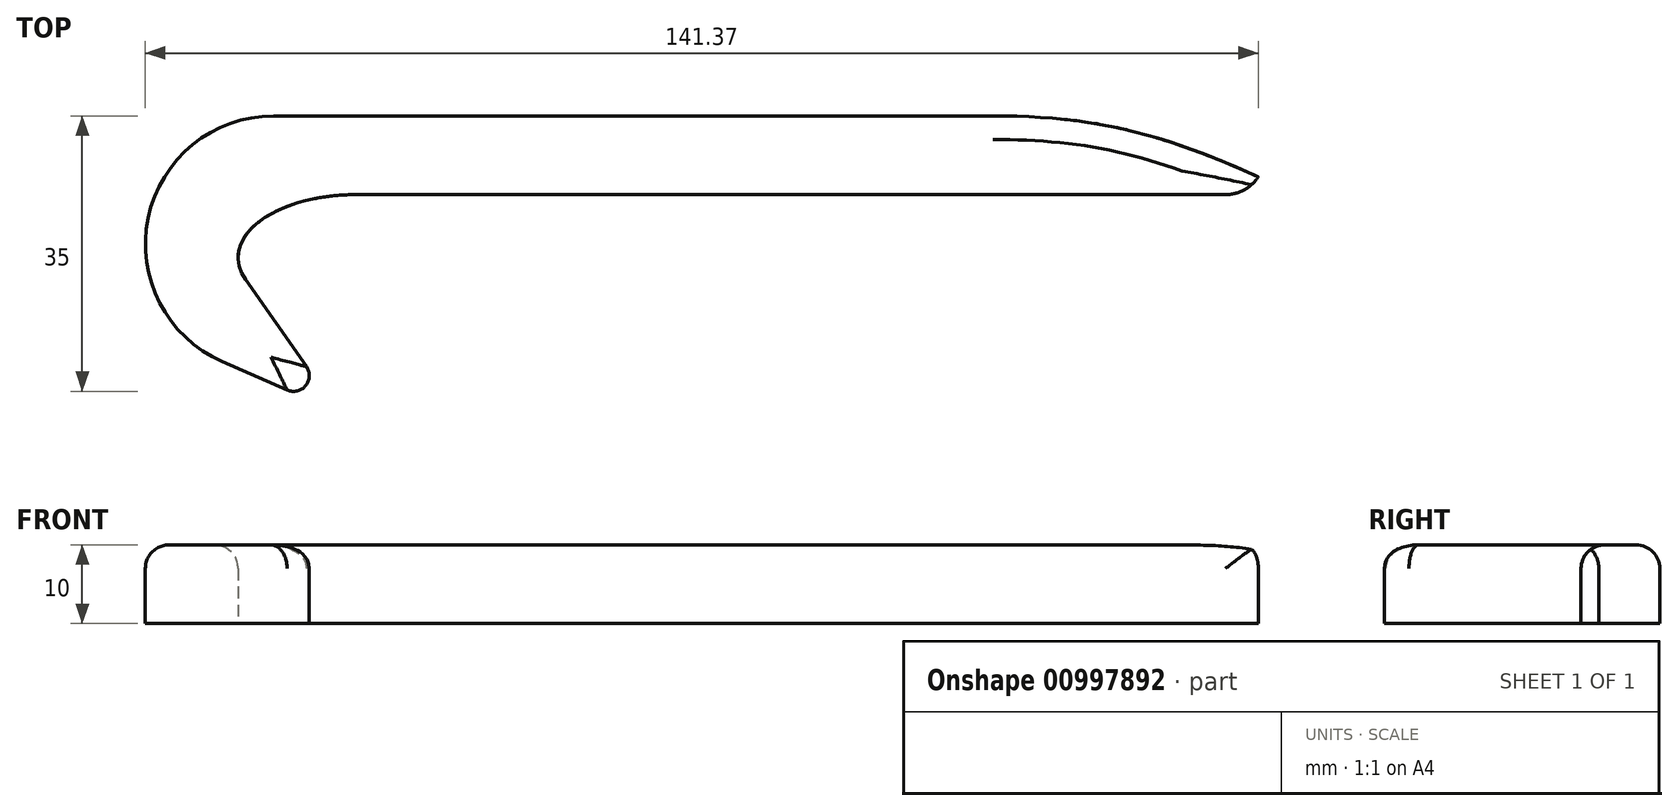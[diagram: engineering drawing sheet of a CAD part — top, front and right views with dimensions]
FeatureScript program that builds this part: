
annotation { "Feature Type Name" : "Feature", "Feature Type Description" : "" }
export const myFeature = defineFeature(function(context is Context, id is Id, definition is map)
    precondition{}
    {
        {
            var Q0;
            Q0=qCreatedBy(makeId("Top.planeOp"),FACE);
            var sketch = newSketch(context, id + "F0", { "sketchPlane" : qUnion([Q0])});
            skLineSegment(sketch, "E0", {"start": v(-59.75, -24.83) * mm, "end": v(-68.01, -21.22) * mm});
            skLineSegment(sketch, "E1", {"start": v(-61.48, 10) * mm, "end": v(0, 10) * mm});
            skLineSegment(sketch, "E2", {"start": v(0, 0) * mm, "end": v(-63.6, 0) * mm});
            skLineSegment(sketch, "E3", {"start": v(-68.12, -6.42) * mm, "end": v(-57.31, -21.85) * mm});
            skPoint(sketch, "E4.visualSharp", {"position": v(-139.32, 10) * mm});
            skArc(sketch, "E4.filletArc", {"start": v(-61.48, 10) * mm, "mid": v(-77.42, -2.95) * mm, "end": v(-68.01, -21.22) * mm});
            skPoint(sketch, "E5.visualSharp", {"position": v(-53.23, -27.69) * mm});
            skArc(sketch, "E5.filletArc", {"start": v(-59.75, -24.83) * mm, "mid": v(-57.4, -24.27) * mm, "end": v(-57.31, -21.85) * mm});
            skPoint(sketch, "E6.visualSharp", {"position": v(-72.61, 0) * mm});
            skLineSegment(sketch, "E7", {"start": v(-36.97, -25) * mm, "end": v(-18.83, -25) * mm, "construction": true});
            skPoint(sketch, "E7.startSnap0", {"position": v(-57.4, -24.27) * mm});
            skLineSegment(sketch, "E8.MirrorCS", {"start": v(0, 0) * mm, "end": v(63.6, 0) * mm});
            skLineSegment(sketch, "E9", {"start": v(0, 10) * mm, "end": v(29.9, 10) * mm});
            skLineSegment(sketch, "E10", {"start": v(63.6, 10) * mm, "end": v(63.6, 0) * mm});
            skEllipse(sketch, "E11", {"center": v(51, -8) * mm, "majorRadius": 15 * mm, "minorRadius": 8 * mm, "majorAxis": v(1, 0)});
            skFitSpline(sketch, "E12.0", {"points": [v(70.9, -9.71) * mm, v(71.05, -8) * mm, v(70.9, -6.29) * mm, v(70.44, -4.67) * mm, v(69.73, -3.18) * mm, v(68.84, -1.85) * mm, v(67.78, -0.67) * mm, v(66.21, 0.73) * mm, v(64.01, 2.14) * mm, v(61.55, 3.2) * mm, v(59.45, 3.88) * mm, v(57.28, 4.43) * mm, v(55.03, 4.79) * mm, v(52.74, 4.97) * mm, v(51, 5.02) * mm, v(49.26, 4.97) * mm, v(46.97, 4.79) * mm, v(44.72, 4.43) * mm, v(42.55, 3.88) * mm, v(40.45, 3.2) * mm, v(37.99, 2.14) * mm, v(35.79, 0.73) * mm, v(34.22, -0.67) * mm, v(33.16, -1.85) * mm, v(32.27, -3.18) * mm, v(31.56, -4.67) * mm, v(31.1, -6.29) * mm, v(30.95, -8) * mm, v(31.1, -9.71) * mm, v(31.56, -11.33) * mm, v(32.27, -12.82) * mm, v(33.16, -14.15) * mm, v(34.22, -15.33) * mm, v(35.79, -16.73) * mm, v(37.99, -18.14) * mm, v(40.45, -19.2) * mm, v(42.55, -19.88) * mm, v(44.72, -20.43) * mm, v(46.97, -20.79) * mm, v(49.26, -20.97) * mm, v(51, -21.02) * mm, v(52.74, -20.97) * mm, v(55.03, -20.79) * mm, v(57.28, -20.43) * mm, v(59.45, -19.88) * mm, v(61.55, -19.2) * mm, v(64.01, -18.14) * mm, v(66.21, -16.73) * mm, v(67.78, -15.33) * mm, v(68.84, -14.15) * mm, v(69.73, -12.82) * mm, v(70.44, -11.33) * mm, v(70.9, -9.71) * mm, v(71.05, -8) * mm, v(70.9, -6.29) * mm]});
            skPoint(sketch, "E13", {"position": v(71, -8) * mm});
            skPoint(sketch, "E13.positionSnap0", {"position": v(66, -8) * mm});
            skPoint(sketch, "E14", {"position": v(63.6, 2.26) * mm});
            skFitSpline(sketch, "E15", {"points": [v(63.6, 2.26) * mm, v(29.9, 10) * mm], "startDerivative": vector(-39.58, 18.02) * mm, "endDerivative": vector(-35.3, 0) * mm});
            skEllipticalArc(sketch, "E16.MirrorC", {});
            skPoint(sketch, "E17", {"position": v(-51, 0) * mm});
            skLineSegment(sketch, "E18", {"start": v(-66, -2.28) * mm, "end": v(-66, -12.03) * mm, "construction": true});
            const initialGuessF0  = {"E16.MirrorC": [-0.051, -0.008, -1, 0, 0.015, 0.008, 4.71238898038469, 0.3574058264075204]};
            skSetInitialGuess(sketch, initialGuessF0);
            skSolve(sketch);
        }
        {
            var Q0;
            Q0=makeQuery(id+"F0.imprint","IMPRINT",FACE,{"disambiguationData":[TD([[makeQuery(id+"F0.imprint","IMPRINT",EDGE,{"derivedFrom":sQuery(id+"F0.wireOp",EDGE,"E0")}),-1.0]])]});
            var Q1;
            {var subQ0=sQuery(id+"F0.wireOp",EDGE,"E11");Q1=makeQuery(id+"F0.imprint","IMPRINT",FACE,{"disambiguationData":[TD([[makeQuery(id+"F0.imprint","IMPRINT",EDGE,{"derivedFrom":subQ0}),-1.0]])]});}
            var Q2;
            {var subQ0=sQuery(id+"F0.wireOp",EDGE,"E12.0");var subQ1=sQuery(id+"F0.wireOp",EDGE,"E8.MirrorCS");var subQ2=makeQuery(id+"F0.imprint","INTERSECT",VERTEX,{"derivedFrom":[subQ1,subQ0]});Q2=makeQuery(id+"F0.imprint","IMPRINT",FACE,{"disambiguationData":[TD([[makeQuery(id+"F0.imprint","IMPRINT",EDGE,{"disambiguationData":[TD([[subQ2,-1.0]])],"derivedFrom":subQ1}),1.0]])]});}
            extrude(context, id + "F1", {"entities" : qUnion([Q0, Q1, Q2]), "depth" : 10 * mm, "offsetDistance" : 25 * mm});
        }
        {
            var Q0;
            Q0=makeQuery(id+"F1.opExtrude","SWEPT_EDGE",EDGE,{"disambiguationData":[OSD([sQuery(id+"F0.wireOp",EDGE,"E8.MirrorCS"),sQuery(id+"F0.wireOp",EDGE,"E12.0")])]});
            fillet(context, id + "F2", {"entities" : qUnion([Q0]), "radius" : 5 * mm, "tangentPropagation" : true, "allowEdgeOverflow" : false});
        }
        {
            var Q0;
            Q0=makeQuery(id+"F1.opExtrude","CAP_EDGE",EDGE,{"disambiguationData":[OSD([sQuery(id+"F0.wireOp",EDGE,"E1"),sQuery(id+"F0.wireOp",EDGE,"E9")])],"isStart":false});
            fillet(context, id + "F3", {"entities" : qUnion([Q0]), "radius" : 3 * mm, "tangentPropagation" : true, "allowEdgeOverflow" : false});
        }
    });
